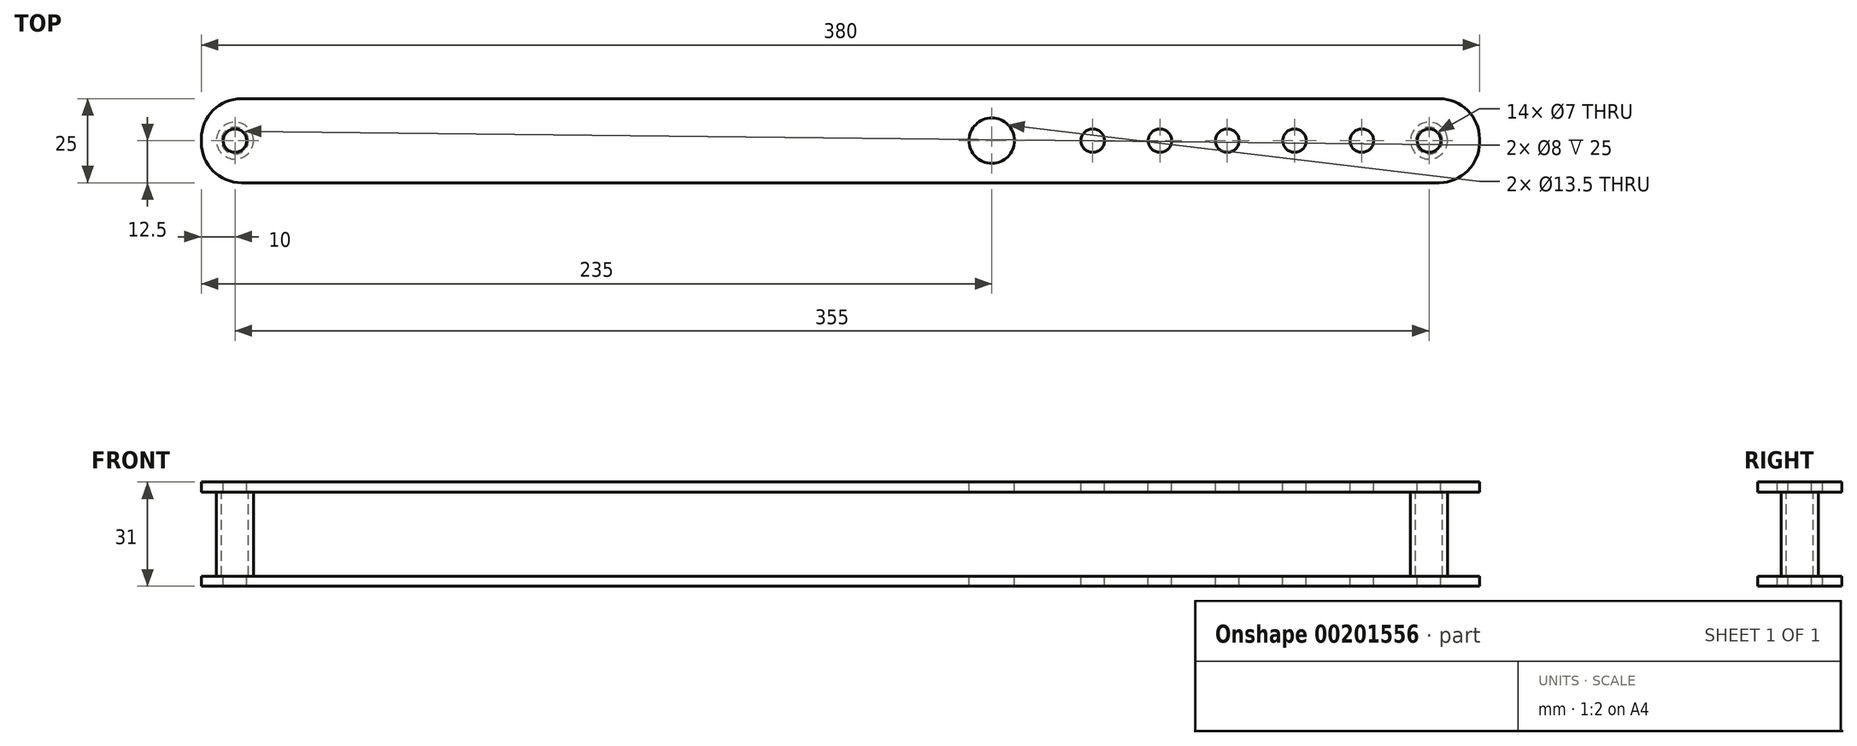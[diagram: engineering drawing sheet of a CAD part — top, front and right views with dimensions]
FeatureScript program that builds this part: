
annotation { "Feature Type Name" : "Feature", "Feature Type Description" : "" }
export const myFeature = defineFeature(function(context is Context, id is Id, definition is map)
    precondition{}
    {
        {
            var Q0;
            Q0=qCreatedBy(makeId("Front.planeOp"),FACE);
            var sketch = newSketch(context, id + "F0", { "sketchPlane" : qUnion([Q0])});
            skLineSegment(sketch, "E0.bottom", {"start": v(0, 0) * mm, "end": v(380, 0) * mm});
            skLineSegment(sketch, "E0.top", {"start": v(0, 3) * mm, "end": v(380, 3) * mm});
            skLineSegment(sketch, "E0.left", {"start": v(0, 0) * mm, "end": v(0, 3) * mm});
            skLineSegment(sketch, "E0.right", {"start": v(380, 0) * mm, "end": v(380, 3) * mm});
            skLineSegment(sketch, "E1", {"start": v(0, 3) * mm, "end": v(0, 28) * mm, "construction": true});
            skLineSegment(sketch, "E2.bottom", {"start": v(0, 28) * mm, "end": v(380, 28) * mm});
            skLineSegment(sketch, "E2.top", {"start": v(0, 31) * mm, "end": v(380, 31) * mm});
            skLineSegment(sketch, "E2.left", {"start": v(0, 28) * mm, "end": v(0, 31) * mm});
            skLineSegment(sketch, "E2.right", {"start": v(380, 28) * mm, "end": v(380, 31) * mm});
            skSolve(sketch);
        }
        {
            var Q0;
            Q0=makeQuery(id+"F0.imprint","IMPRINT",FACE,{"disambiguationData":[TD([[makeQuery(id+"F0.imprint","IMPRINT",EDGE,{"derivedFrom":sQuery(id+"F0.wireOp",EDGE,"E2.bottom")}),1.0]])]});
            var Q1;
            Q1=makeQuery(id+"F0.imprint","IMPRINT",FACE,{"disambiguationData":[TD([[makeQuery(id+"F0.imprint","IMPRINT",EDGE,{"derivedFrom":sQuery(id+"F0.wireOp",EDGE,"E0.bottom")}),1.0]])]});
            extrude(context, id + "F1", {"entities" : qUnion([Q0, Q1]), "depth" : 25 * mm, "offsetDistance" : 25 * mm});
        }
        {
            var Q0;
            Q0=makeQuery(id+"F1.opExtrude","CAP_EDGE",EDGE,{"disambiguationData":[OSD([sQuery(id+"F0.wireOp",EDGE,"E2.right")])],"isStart":false});
            var Q1;
            Q1=makeQuery(id+"F1.opExtrude","CAP_EDGE",EDGE,{"disambiguationData":[OSD([sQuery(id+"F0.wireOp",EDGE,"E2.right")])],"isStart":true});
            var Q2;
            Q2=makeQuery(id+"F1.opExtrude","CAP_EDGE",EDGE,{"disambiguationData":[OSD([sQuery(id+"F0.wireOp",EDGE,"E0.right")])],"isStart":true});
            var Q3;
            Q3=makeQuery(id+"F1.opExtrude","CAP_EDGE",EDGE,{"disambiguationData":[OSD([sQuery(id+"F0.wireOp",EDGE,"E0.right")])],"isStart":false});
            var Q4;
            Q4=makeQuery(id+"F1.opExtrude","CAP_EDGE",EDGE,{"disambiguationData":[OSD([sQuery(id+"F0.wireOp",EDGE,"E2.left")])],"isStart":false});
            var Q5;
            Q5=makeQuery(id+"F1.opExtrude","CAP_EDGE",EDGE,{"disambiguationData":[OSD([sQuery(id+"F0.wireOp",EDGE,"E2.left")])],"isStart":true});
            var Q6;
            Q6=makeQuery(id+"F1.opExtrude","CAP_EDGE",EDGE,{"disambiguationData":[OSD([sQuery(id+"F0.wireOp",EDGE,"E0.left")])],"isStart":true});
            var Q7;
            Q7=makeQuery(id+"F1.opExtrude","CAP_EDGE",EDGE,{"disambiguationData":[OSD([sQuery(id+"F0.wireOp",EDGE,"E0.left")])],"isStart":false});
            fillet(context, id + "F2", {"entities" : qUnion([Q0, Q1, Q2, Q3, Q4, Q5, Q6, Q7]), "radius" : 12 * mm, "tangentPropagation" : true, "allowEdgeOverflow" : false});
        }
        {
            var Q0;
            Q0=makeQuery(id+"F1.opExtrude","SWEPT_FACE",FACE,{"disambiguationData":[OSD([sQuery(id+"F0.wireOp",EDGE,"E2.top")])]});
            var sketch = newSketch(context, id + "F3", { "sketchPlane" : qUnion([Q0])});
            skLineSegment(sketch, "E3", {"start": v(0, -12.5) * mm, "end": v(380, -12.5) * mm, "construction": true});
            skLineSegment(sketch, "E4", {"start": v(10, -12.5) * mm, "end": v(10, 10.6) * mm, "construction": true});
            skCircle(sketch, "E5", {"center": v(10, -12.5) * mm, "radius": 3.5 * mm});
            skLineSegment(sketch, "E6", {"start": v(235, -12.5) * mm, "end": v(235, 30.68) * mm, "construction": true});
            skCircle(sketch, "E7", {"center": v(235, -12.5) * mm, "radius": 6.75 * mm});
            skLineSegment(sketch, "E8", {"start": v(365, -12.5) * mm, "end": v(365, 22.52) * mm, "construction": true});
            skCircle(sketch, "E9", {"center": v(365, -12.5) * mm, "radius": 3.5 * mm});
            skCircle(sketch, "E10", {"center": v(10, -12.5) * mm, "radius": 5.5 * mm});
            skCircle(sketch, "E11", {"center": v(10, -12.5) * mm, "radius": 4 * mm});
            skCircle(sketch, "E12", {"center": v(365, -12.5) * mm, "radius": 5.5 * mm});
            skCircle(sketch, "E13", {"center": v(365, -12.5) * mm, "radius": 4 * mm});
            skLineSegment(sketch, "E14", {"start": v(285, -12.5) * mm, "end": v(285, 12.5) * mm, "construction": true});
            skLineSegment(sketch, "E15", {"start": v(305, -12.5) * mm, "end": v(305, 12.5) * mm, "construction": true});
            skLineSegment(sketch, "E16", {"start": v(325, -12.5) * mm, "end": v(325, 12.5) * mm, "construction": true});
            skLineSegment(sketch, "E17", {"start": v(345, -12.5) * mm, "end": v(345, 12.5) * mm, "construction": true});
            skLineSegment(sketch, "E18", {"start": v(265, -12.5) * mm, "end": v(265, 12.5) * mm, "construction": true});
            skCircle(sketch, "E19", {"center": v(265, -12.5) * mm, "radius": 3.5 * mm});
            skCircle(sketch, "E20", {"center": v(285, -12.5) * mm, "radius": 3.5 * mm});
            skCircle(sketch, "E21", {"center": v(305, -12.5) * mm, "radius": 3.5 * mm});
            skCircle(sketch, "E22", {"center": v(325, -12.5) * mm, "radius": 3.5 * mm});
            skCircle(sketch, "E23", {"center": v(345, -12.5) * mm, "radius": 3.5 * mm});
            skSolve(sketch);
        }
        {
            var Q0;
            Q0=makeQuery(id+"F3.imprint","IMPRINT",FACE,{"disambiguationData":[TD([[makeQuery(id+"F3.imprint","IMPRINT",EDGE,{"derivedFrom":sQuery(id+"F3.wireOp",EDGE,"E5")}),1.0]])]});
            var Q1;
            Q1=makeQuery(id+"F3.imprint","IMPRINT",FACE,{"disambiguationData":[TD([[makeQuery(id+"F3.imprint","IMPRINT",EDGE,{"derivedFrom":sQuery(id+"F3.wireOp",EDGE,"E7")}),1.0]])]});
            var Q2;
            Q2=makeQuery(id+"F3.imprint","IMPRINT",FACE,{"disambiguationData":[TD([[makeQuery(id+"F3.imprint","IMPRINT",EDGE,{"derivedFrom":sQuery(id+"F3.wireOp",EDGE,"E9")}),1.0]])]});
            var Q3;
            Q3=makeQuery(id+"F3.imprint","IMPRINT",FACE,{"disambiguationData":[TD([[makeQuery(id+"F3.imprint","IMPRINT",EDGE,{"derivedFrom":sQuery(id+"F3.wireOp",EDGE,"E19")}),1.0]])]});
            var Q4;
            Q4=makeQuery(id+"F3.imprint","IMPRINT",FACE,{"disambiguationData":[TD([[makeQuery(id+"F3.imprint","IMPRINT",EDGE,{"derivedFrom":sQuery(id+"F3.wireOp",EDGE,"E20")}),1.0]])]});
            var Q5;
            Q5=makeQuery(id+"F3.imprint","IMPRINT",FACE,{"disambiguationData":[TD([[makeQuery(id+"F3.imprint","IMPRINT",EDGE,{"derivedFrom":sQuery(id+"F3.wireOp",EDGE,"E21")}),1.0]])]});
            var Q6;
            Q6=makeQuery(id+"F3.imprint","IMPRINT",FACE,{"disambiguationData":[TD([[makeQuery(id+"F3.imprint","IMPRINT",EDGE,{"derivedFrom":sQuery(id+"F3.wireOp",EDGE,"E22")}),1.0]])]});
            var Q7;
            Q7=makeQuery(id+"F3.imprint","IMPRINT",FACE,{"disambiguationData":[TD([[makeQuery(id+"F3.imprint","IMPRINT",EDGE,{"derivedFrom":sQuery(id+"F3.wireOp",EDGE,"E23")}),1.0]])]});
            extrude(context, id + "F4", {"entities" : qUnion([Q0, Q1, Q2, Q3, Q4, Q5, Q6, Q7]), "operationType" : NewBodyOperationType.REMOVE, "oppositeDirection" : true, "depth" : 35 * mm, "offsetDistance" : 25 * mm});
        }
        {
            var Q0;
            Q0=makeQuery(id+"F3.imprint","IMPRINT",FACE,{"disambiguationData":[TD([[makeQuery(id+"F3.imprint","IMPRINT",EDGE,{"derivedFrom":sQuery(id+"F3.wireOp",EDGE,"E10")}),1.0]])]});
            var Q1;
            Q1=makeQuery(id+"F3.imprint","IMPRINT",FACE,{"disambiguationData":[TD([[makeQuery(id+"F3.imprint","IMPRINT",EDGE,{"derivedFrom":sQuery(id+"F3.wireOp",EDGE,"E12")}),1.0]])]});
            var Q2;
            Q2=makeQuery(id+"F1.opExtrude","SWEPT_FACE",FACE,{"disambiguationData":[OSD([sQuery(id+"F0.wireOp",EDGE,"E0.top")])]});
            extrude(context, id + "F5", {"entities" : qUnion([Q0, Q1]), "endBound" : BoundingType.UP_TO_SURFACE, "oppositeDirection" : true, "depth" : 25 * mm, "endBoundEntityFace" : qUnion([Q2]), "offsetDistance" : 30 * mm, "hasSecondDirection" : true, "secondDirectionOppositeDirection" : true, "secondDirectionDepth" : 3 * mm});
        }
    });
